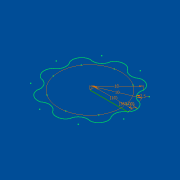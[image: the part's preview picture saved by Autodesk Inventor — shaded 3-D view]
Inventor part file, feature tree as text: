
AUTODESK INVENTOR PART (.ipt)
format: ipt  version: 2016 (Build 200138000, 138)  size: 72,704 bytes
history: native  units: mm
features: sketch x1
ambient origin geometry x8: Origin, YZ Plane, XZ Plane, XY Plane, X Axis, Y Axis, Z Axis, Center Point
feature tree (1):
  sketch  "Sketch1"  dims[d0=10.0mm d2=10.0mm d4=10.0mm d5=2.5mm d6=2.5mm d7=80.0mm d9=360.0deg]
